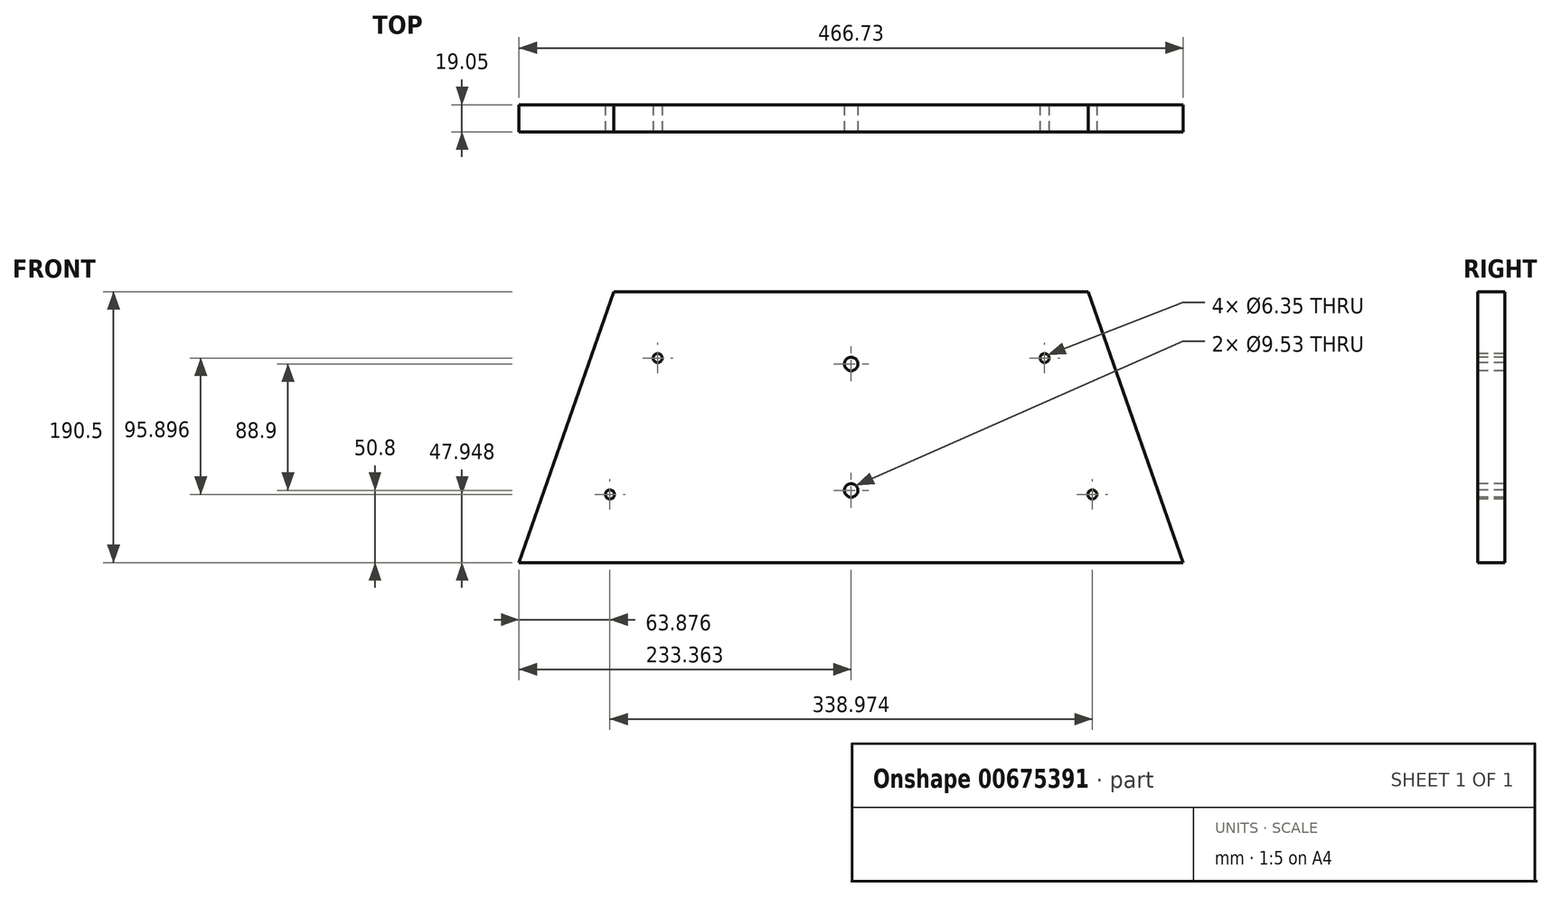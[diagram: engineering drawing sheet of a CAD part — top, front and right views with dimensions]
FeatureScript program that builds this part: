
annotation { "Feature Type Name" : "Feature", "Feature Type Description" : "" }
export const myFeature = defineFeature(function(context is Context, id is Id, definition is map)
    precondition{}
    {
        {
            var Q0;
            Q0=qCreatedBy(makeId("Front.planeOp"),FACE);
            var sketch = newSketch(context, id + "F0", { "sketchPlane" : qUnion([Q0])});
            skLineSegment(sketch, "E0", {"start": v(0, 0) * mm, "end": v(466.73, 0) * mm});
            skLineSegment(sketch, "E1", {"start": v(466.73, 0) * mm, "end": v(400.05, 190.5) * mm});
            skLineSegment(sketch, "E2", {"start": v(400.05, 190.5) * mm, "end": v(66.67, 190.5) * mm});
            skLineSegment(sketch, "E3", {"start": v(66.68, 190.5) * mm, "end": v(0, 0) * mm});
            skSolve(sketch);
        }
        {
            var Q0;
            Q0 = qSketchRegion(id + "F0", true);
            extrude(context, id + "F1", {"entities" : qUnion([Q0]), "depth" : 19.05 * mm, "offsetDistance" : 25.4 * mm});
        }
        {
            var Q0;
            Q0=makeQuery(id+"F1.opExtrude","CAP_FACE",FACE,{"disambiguationData":[OSD([sQuery(id+"F0.wireOp",EDGE,"E0"),sQuery(id+"F0.wireOp",EDGE,"E1"),sQuery(id+"F0.wireOp",EDGE,"E2"),sQuery(id+"F0.wireOp",EDGE,"E3")])],"isStart":false});
            var sketch = newSketch(context, id + "F2", { "sketchPlane" : qUnion([Q0])});
            skLineSegment(sketch, "E4", {"start": v(47.1, 0) * mm, "end": v(113.77, 190.5) * mm, "construction": true});
            skLineSegment(sketch, "E5", {"start": v(352.96, 190.5) * mm, "end": v(419.63, 0) * mm, "construction": true});
            skCircle(sketch, "E6", {"center": v(97.44, 143.84) * mm, "radius": 3.18 * mm});
            skCircle(sketch, "E7", {"center": v(63.88, 47.95) * mm, "radius": 3.18 * mm});
            skCircle(sketch, "E8", {"center": v(369.29, 143.84) * mm, "radius": 3.17 * mm});
            skCircle(sketch, "E9", {"center": v(402.85, 47.95) * mm, "radius": 3.18 * mm});
            skLineSegment(sketch, "E10", {"start": v(233.36, 190.5) * mm, "end": v(233.36, 0) * mm, "construction": true});
            skCircle(sketch, "E11", {"center": v(233.36, 139.7) * mm, "radius": 4.76 * mm});
            skCircle(sketch, "E12", {"center": v(233.36, 50.8) * mm, "radius": 4.76 * mm});
            skSolve(sketch);
        }
        {
            var Q0;
            Q0 = qSketchRegion(id + "F2", true);
            extrude(context, id + "F3", {"entities" : qUnion([Q0]), "operationType" : NewBodyOperationType.REMOVE, "oppositeDirection" : true, "depth" : 25.4 * mm, "offsetDistance" : 25.4 * mm});
        }
    });
